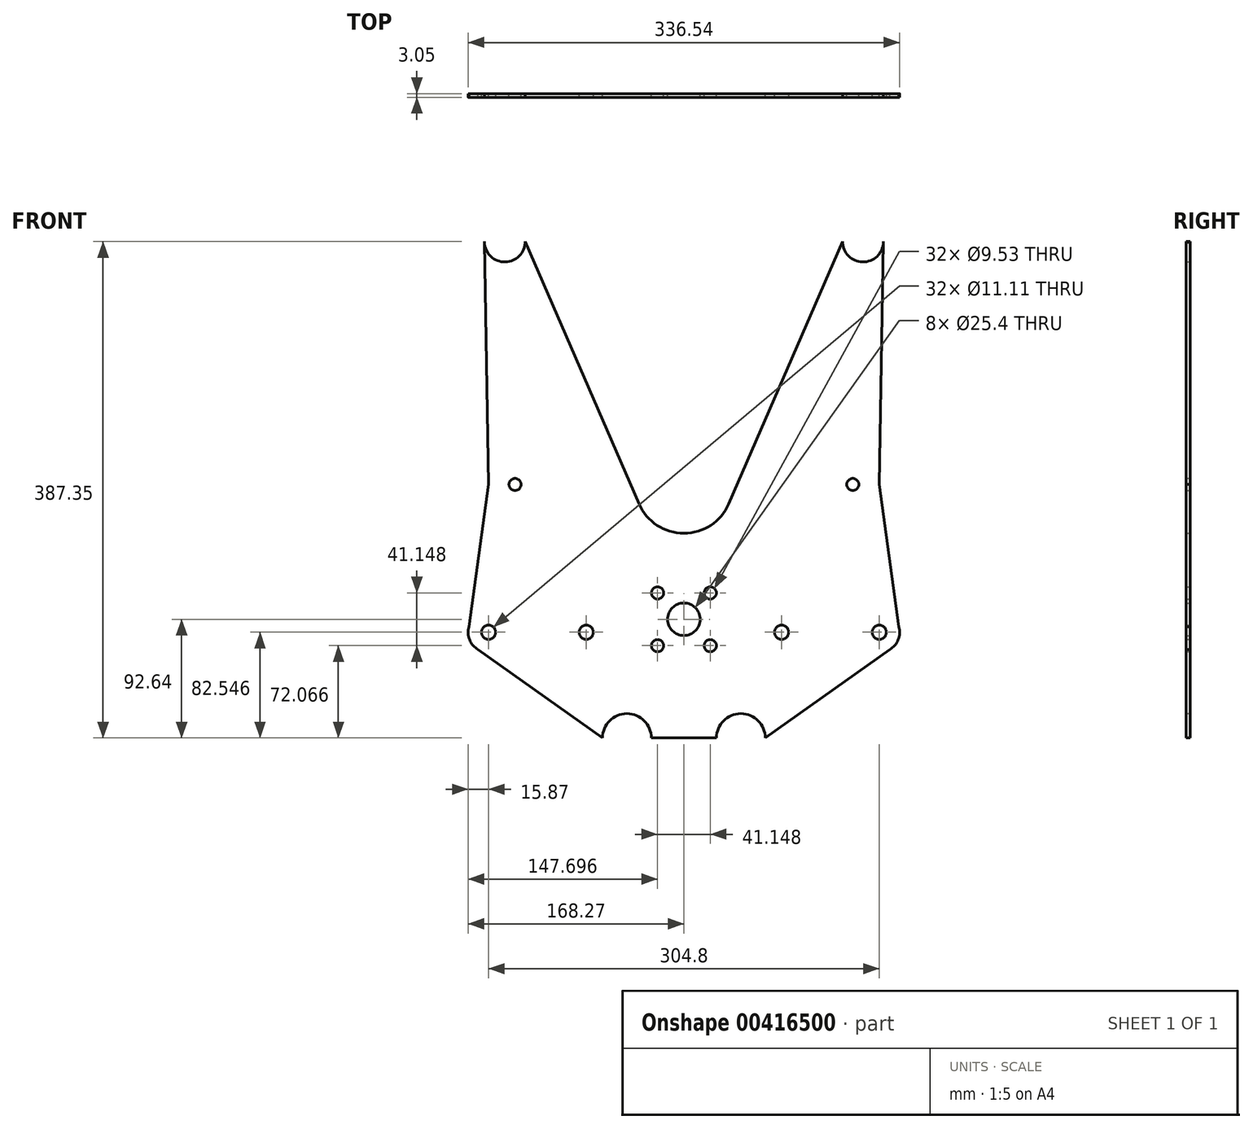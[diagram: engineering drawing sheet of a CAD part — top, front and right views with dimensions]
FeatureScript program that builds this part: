
annotation { "Feature Type Name" : "Feature", "Feature Type Description" : "" }
export const myFeature = defineFeature(function(context is Context, id is Id, definition is map)
    precondition{}
    {
        {
            var Q0;
            Q0=qCreatedBy(makeId("Front.planeOp"),FACE);
            var sketch = newSketch(context, id + "F0", { "sketchPlane" : qUnion([Q0])});
            skCircle(sketch, "E0", {"center": v(0, 0) * mm, "radius": 12.7 * mm});
            skLineSegment(sketch, "E1.bottom", {"start": v(20.57, -20.57) * mm, "end": v(-20.57, -20.57) * mm, "construction": true});
            skLineSegment(sketch, "E1.top", {"start": v(20.57, 20.57) * mm, "end": v(-20.57, 20.57) * mm, "construction": true});
            skLineSegment(sketch, "E1.left", {"start": v(20.57, -20.57) * mm, "end": v(20.57, 20.57) * mm, "construction": true});
            skLineSegment(sketch, "E1.right", {"start": v(-20.57, -20.57) * mm, "end": v(-20.57, 20.57) * mm, "construction": true});
            skCircle(sketch, "E2", {"center": v(-20.57, 20.57) * mm, "radius": 4.76 * mm});
            skCircle(sketch, "E3", {"center": v(20.57, 20.57) * mm, "radius": 4.76 * mm});
            skCircle(sketch, "E4", {"center": v(20.57, -20.57) * mm, "radius": 4.76 * mm});
            skCircle(sketch, "E5", {"center": v(-20.57, -20.57) * mm, "radius": 4.76 * mm});
            skPoint(sketch, "E6", {"position": v(20.57, -15.81) * mm});
            skPoint(sketch, "E7", {"position": v(-20.57, -15.81) * mm});
            skLineSegment(sketch, "E8", {"start": v(0, -15.81) * mm, "end": v(152.4, -15.81) * mm, "construction": true});
            skPoint(sketch, "E8.startSnap0", {"position": v(0, -20.57) * mm});
            skLineSegment(sketch, "E9", {"start": v(0, -15.81) * mm, "end": v(-152.4, -15.81) * mm, "construction": true});
            skCircle(sketch, "E10", {"center": v(-152.4, -10.1) * mm, "radius": 5.56 * mm});
            skCircle(sketch, "E11", {"center": v(152.4, -10.1) * mm, "radius": 5.56 * mm});
            skCircle(sketch, "E12", {"center": v(76.2, -10.1) * mm, "radius": 5.56 * mm});
            skCircle(sketch, "E13", {"center": v(-76.2, -10.1) * mm, "radius": 5.56 * mm});
            skPoint(sketch, "E14", {"position": v(-152.4, 105.22) * mm});
            skLineSegment(sketch, "E15", {"start": v(0, 0) * mm, "end": v(0, 140.85) * mm, "construction": true});
            skPoint(sketch, "E15.endSnap0", {"position": v(0, 20.57) * mm});
            skLineSegment(sketch, "E16", {"start": v(-152.4, -10.1) * mm, "end": v(-152.4, -92.64) * mm, "construction": true});
            skLineSegment(sketch, "E17", {"start": v(-152.4, -10.1) * mm, "end": v(-152.4, 294.7) * mm, "construction": true});
            skLineSegment(sketch, "E18", {"start": v(-152.4, 105.22) * mm, "end": v(152.4, 105.22) * mm, "construction": true});
            skCircle(sketch, "E19", {"center": v(-131.75, 105.22) * mm, "radius": 4.72 * mm});
            skCircle(sketch, "E20", {"center": v(131.75, 105.22) * mm, "radius": 4.7 * mm});
            skLineSegment(sketch, "E21", {"start": v(-152.4, -92.64) * mm, "end": v(152.4, -92.64) * mm, "construction": true});
            skPoint(sketch, "E22", {"position": v(-44.45, -92.64) * mm});
            skLineSegment(sketch, "E23", {"start": v(0, -20.57) * mm, "end": v(0, -115.22) * mm, "construction": true});
            skPoint(sketch, "E24", {"position": v(44.45, -92.64) * mm});
            skArc(sketch, "E25", {"start": v(-25.4, -92.64) * mm, "mid": v(-44.45, -73.6) * mm, "end": v(-63.5, -92.64) * mm});
            skArc(sketch, "E26", {"start": v(63.5, -92.64) * mm, "mid": v(44.45, -73.6) * mm, "end": v(25.4, -92.64) * mm});
            skLineSegment(sketch, "E27", {"start": v(-25.4, -92.64) * mm, "end": v(25.4, -92.64) * mm});
            skLineSegment(sketch, "E28", {"start": v(0, 0) * mm, "end": v(0, 293.77) * mm, "construction": true});
            skLineSegment(sketch, "E29", {"start": v(152.4, 294.7) * mm, "end": v(-152.4, 294.7) * mm, "construction": true});
            skPoint(sketch, "E30", {"position": v(-139.7, 294.7) * mm});
            skPoint(sketch, "E31", {"position": v(139.7, 294.7) * mm});
            skArc(sketch, "E32", {"start": v(-155.58, 294.7) * mm, "mid": v(-155.57, 294.44) * mm, "end": v(-155.57, 294.17) * mm});
            skArc(sketch, "E33", {"start": v(155.57, 294.17) * mm, "mid": v(155.57, 294.44) * mm, "end": v(155.58, 294.7) * mm});
            skArc(sketch, "E34", {"start": v(160.54, -23.72) * mm, "mid": v(167.15, -15.97) * mm, "end": v(167.68, -5.8) * mm});
            skArc(sketch, "E35", {"start": v(-167.68, -5.8) * mm, "mid": v(-167.15, -15.97) * mm, "end": v(-160.54, -23.72) * mm});
            skLineSegment(sketch, "E36", {"start": v(155.58, 294.7) * mm, "end": v(155.57, 294.17) * mm});
            skLineSegment(sketch, "E37", {"start": v(152.4, 105.22) * mm, "end": v(168.28, -10.1) * mm});
            skLineSegment(sketch, "E38", {"start": v(-155.58, 294.7) * mm, "end": v(-152.4, 105.22) * mm});
            skLineSegment(sketch, "E39", {"start": v(-152.4, 105.22) * mm, "end": v(-168.28, -10.1) * mm});
            skLineSegment(sketch, "E40", {"start": v(155.58, 294.7) * mm, "end": v(152.4, 105.22) * mm});
            skLineSegment(sketch, "E41", {"start": v(162.59, -22.27) * mm, "end": v(63.5, -92.64) * mm});
            skLineSegment(sketch, "E42", {"start": v(-162.59, -22.27) * mm, "end": v(-63.5, -92.64) * mm});
            skPoint(sketch, "E43.orphan", {"position": v(-25.4, 196.65) * mm});
            skPoint(sketch, "E44.center.orphan", {"position": v(0, 196.65) * mm});
            skPoint(sketch, "E45.end.orphan", {"position": v(25.4, 196.65) * mm});
            skArc(sketch, "E46", {"start": v(-34.95, 90.05) * mm, "mid": v(0, 67.12) * mm, "end": v(34.95, 90.05) * mm});
            skLineSegment(sketch, "E47", {"start": v(-123.83, 294.7) * mm, "end": v(-34.95, 90.05) * mm});
            skLineSegment(sketch, "E48", {"start": v(123.83, 294.7) * mm, "end": v(34.95, 90.05) * mm});
            skArc(sketch, "E49", {"start": v(-155.58, 294.7) * mm, "mid": v(-139.7, 278.83) * mm, "end": v(-123.83, 294.7) * mm});
            skArc(sketch, "E50", {"start": v(123.83, 294.7) * mm, "mid": v(139.7, 278.83) * mm, "end": v(155.58, 294.7) * mm});
            skSolve(sketch);
        }
        {
            var Q0;
            Q0=qSketchRegion(id+"F0",true);
            extrude(context, id + "F1", {"entities" : qUnion([Q0]), "depth" : 3.05 * mm});
        }
        {
            var Q0;
            Q0 = qSketchRegion(id + "F0", true);
            extrude(context, id + "F2", {"entities" : qUnion([Q0]), "depth" : 3.05 * mm});
        }
    });
